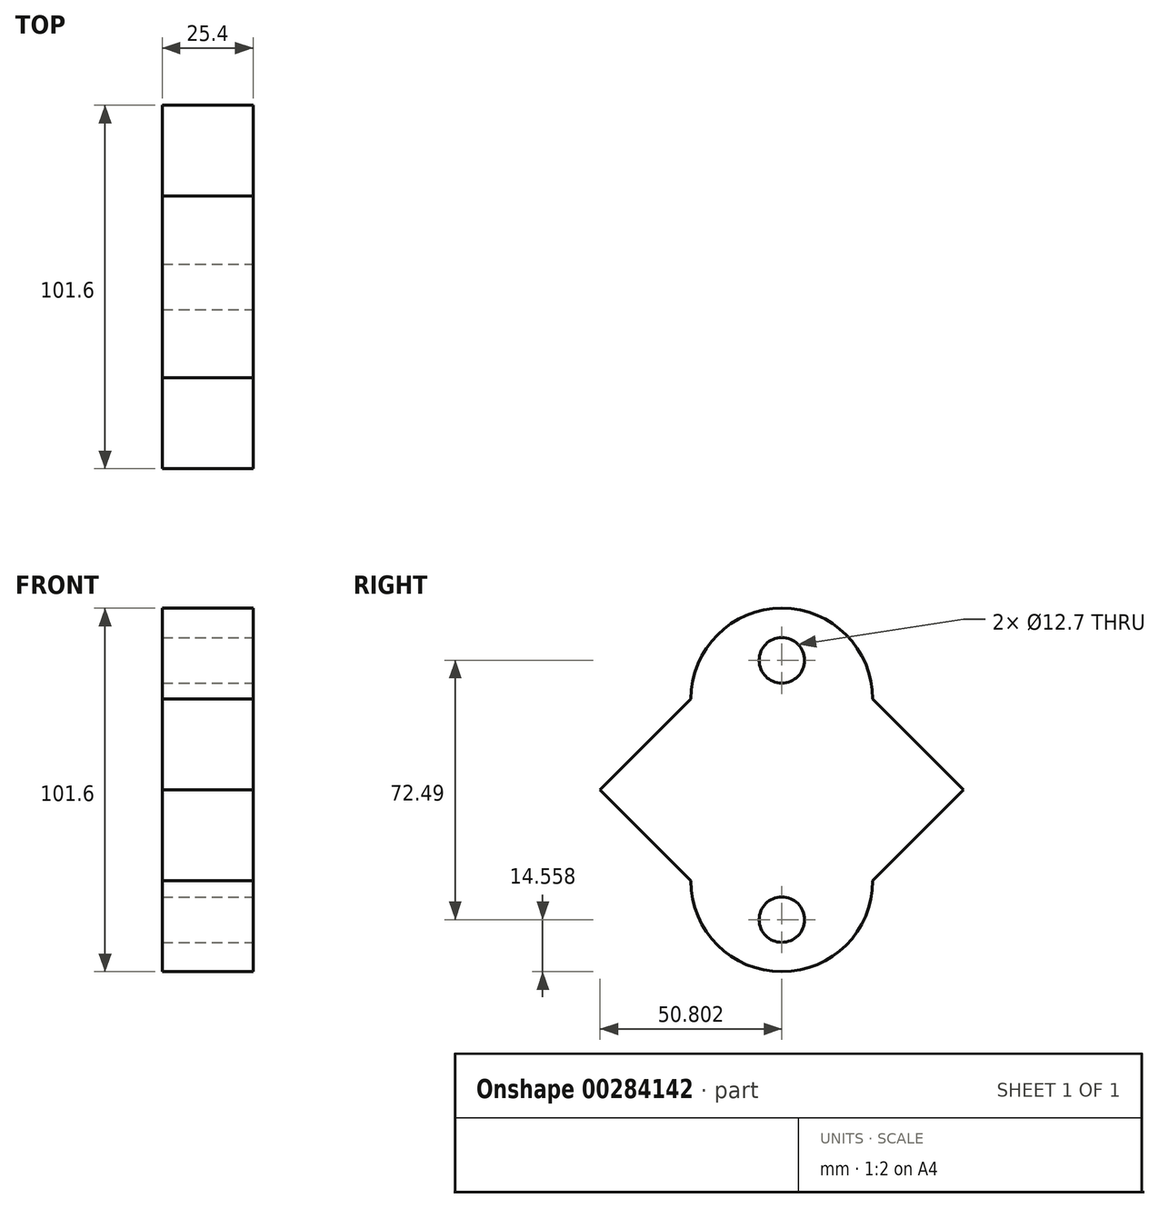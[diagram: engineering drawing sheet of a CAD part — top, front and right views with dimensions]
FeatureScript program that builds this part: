
annotation { "Feature Type Name" : "Feature", "Feature Type Description" : "" }
export const myFeature = defineFeature(function(context is Context, id is Id, definition is map)
    precondition{}
    {
        {
            var Q0;
            Q0=qCreatedBy(makeId("Right.planeOp"),FACE);
            var sketch = newSketch(context, id + "F0", { "sketchPlane" : qUnion([Q0])});
            skLineSegment(sketch, "E0.bottom", {"start": v(-44.59, 49.31) * mm, "end": v(6.21, 49.31) * mm});
            skLineSegment(sketch, "E0.top", {"start": v(-44.59, -1.49) * mm, "end": v(6.21, -1.49) * mm});
            skLineSegment(sketch, "E0.left", {"start": v(-44.59, 49.31) * mm, "end": v(-44.59, -1.49) * mm});
            skLineSegment(sketch, "E0.right", {"start": v(6.21, 49.31) * mm, "end": v(6.21, -1.49) * mm});
            skArc(sketch, "E1", {"start": v(6.21, 49.31) * mm, "mid": v(-19.19, 74.71) * mm, "end": v(-44.59, 49.31) * mm});
            skArc(sketch, "E2", {"start": v(-44.59, -1.49) * mm, "mid": v(-19.19, -26.89) * mm, "end": v(6.21, -1.49) * mm});
            skLineSegment(sketch, "E3", {"start": v(6.21, 49.31) * mm, "end": v(31.61, 23.91) * mm});
            skLineSegment(sketch, "E4", {"start": v(31.61, 23.91) * mm, "end": v(6.21, -1.49) * mm});
            skLineSegment(sketch, "E5.MirrorCS", {"start": v(-44.59, 49.31) * mm, "end": v(-69.99, 23.91) * mm});
            skLineSegment(sketch, "E6.MirrorCS", {"start": v(-69.99, 23.91) * mm, "end": v(-44.59, -1.49) * mm});
            skSolve(sketch);
        }
        {
            var Q0;
            Q0 = qSketchRegion(id + "F0", true);
            extrude(context, id + "F1", {"entities" : qUnion([Q0]), "depth" : 25.4 * mm});
        }
        {
            var Q0;
            Q0=makeQuery(id+"F1.opExtrude","CAP_FACE",FACE,{"disambiguationData":[OSD([sQuery(id+"F0.wireOp",EDGE,"E1"),sQuery(id+"F0.wireOp",EDGE,"E2"),sQuery(id+"F0.wireOp",EDGE,"E3"),sQuery(id+"F0.wireOp",EDGE,"E4"),sQuery(id+"F0.wireOp",EDGE,"E5.MirrorCS"),sQuery(id+"F0.wireOp",EDGE,"E6.MirrorCS")])],"isStart":false});
            var sketch = newSketch(context, id + "F2", { "sketchPlane" : qUnion([Q0])});
            skLineSegment(sketch, "E7", {"start": v(-44.59, 49.31) * mm, "end": v(6.21, 49.31) * mm});
            skLineSegment(sketch, "E8", {"start": v(6.21, -1.49) * mm, "end": v(6.21, 49.31) * mm});
            skLineSegment(sketch, "E9", {"start": v(-44.59, 49.31) * mm, "end": v(-44.59, -1.49) * mm});
            skLineSegment(sketch, "E10", {"start": v(-44.59, -1.49) * mm, "end": v(6.21, -1.49) * mm});
            skCircle(sketch, "E11", {"center": v(-19.19, 60.16) * mm, "radius": 6.56 * mm});
            skPoint(sketch, "E11.centerSnap0", {"position": v(-19.19, 49.31) * mm});
            skLineSegment(sketch, "E12", {"start": v(-44.59, 23.91) * mm, "end": v(6.21, 23.91) * mm, "construction": true});
            skCircle(sketch, "E13.MirrorC", {"center": v(-19.19, -12.33) * mm, "radius": 6.56 * mm});
            skSolve(sketch);
        }
        {
            var Q0;
            Q0=sQuery(id+"F2.wireOp",VERTEX,"E11.center");
            var Q1;
            Q1=sQuery(id+"F2.wireOp",VERTEX,"E13.MirrorC.center");
            var Q2;
            Q2=makeQuery(id+"F1.opExtrude","SWEPT_BODY",BODY,{"disambiguationData":[OSD([sQuery(id+"F0.wireOp",EDGE,"E1"),sQuery(id+"F0.wireOp",EDGE,"E2"),sQuery(id+"F0.wireOp",EDGE,"E3"),sQuery(id+"F0.wireOp",EDGE,"E4"),sQuery(id+"F0.wireOp",EDGE,"E5.MirrorCS"),sQuery(id+"F0.wireOp",EDGE,"E6.MirrorCS")])]});
            hole(context, id + "F3", {"style" : HoleStyle.SIMPLE, "endStyle" : HoleEndStyle.THROUGH, "holeDiameter" : 12.7 * mm, "tappedDepth" : 12.7 * mm, "tapClearance" : 3, "locations" : qUnion([Q0, Q1]), "scope" : qUnion([Q2])});
        }
    });
